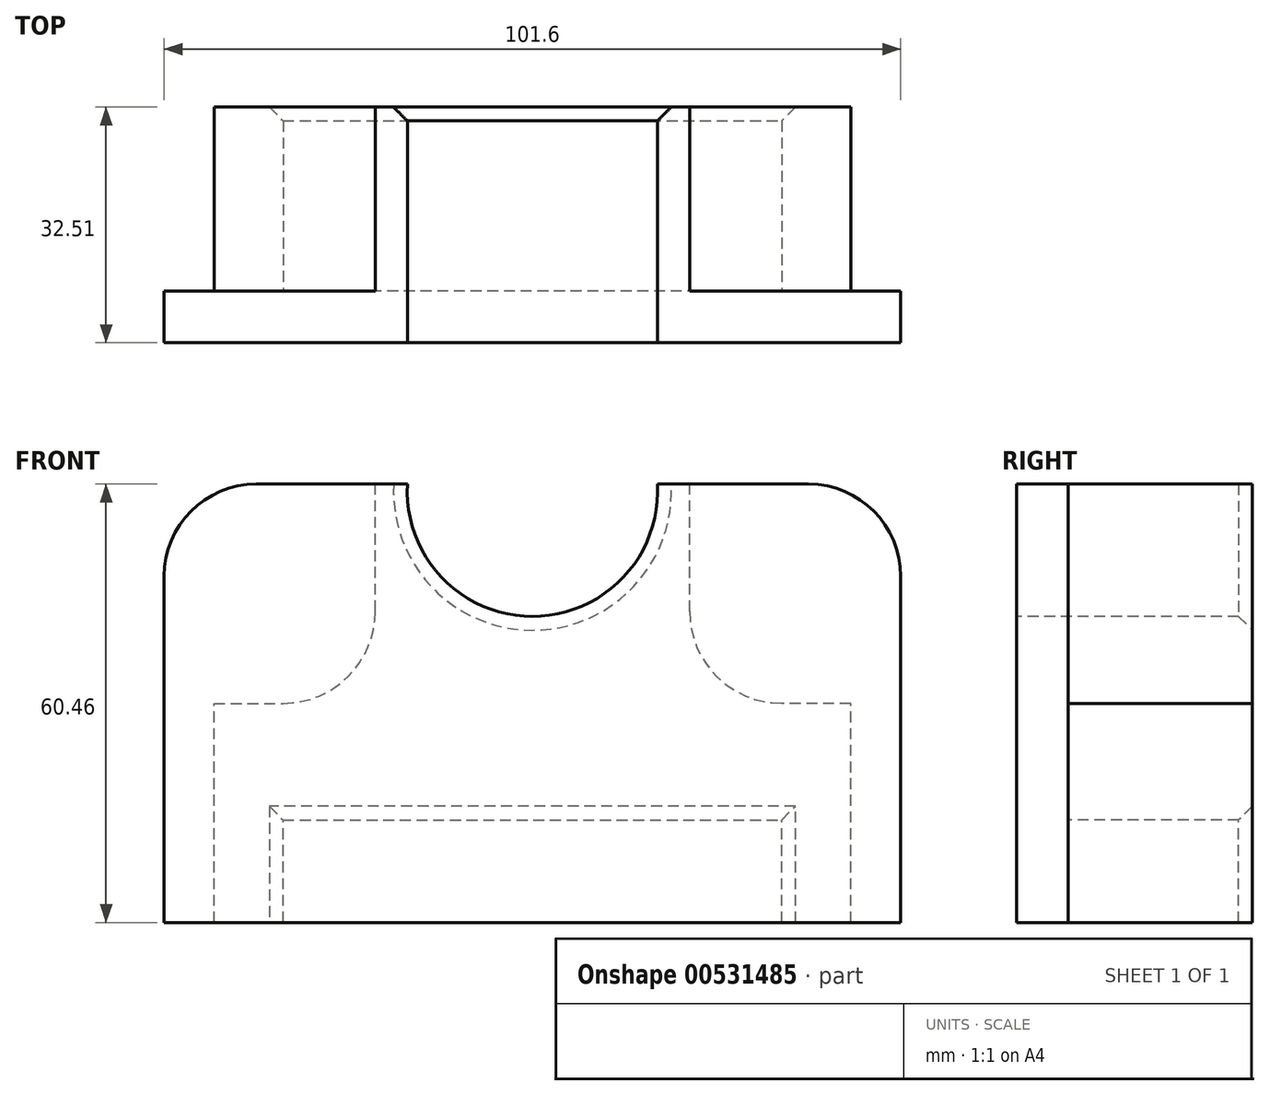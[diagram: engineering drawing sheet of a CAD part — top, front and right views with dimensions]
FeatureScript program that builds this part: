
annotation { "Feature Type Name" : "Feature", "Feature Type Description" : "" }
export const myFeature = defineFeature(function(context is Context, id is Id, definition is map)
    precondition{}
    {
        {
            var Q0;
            Q0=qCreatedBy(makeId("Front.planeOp"),FACE);
            var sketch = newSketch(context, id + "F0", { "sketchPlane" : qUnion([Q0])});
            skLineSegment(sketch, "E0.bottom", {"start": v(50.8, -30.23) * mm, "end": v(-50.8, -30.23) * mm});
            skLineSegment(sketch, "E0.top", {"start": v(38.1, 30.23) * mm, "end": v(-38.1, 30.23) * mm});
            skLineSegment(sketch, "E0.left", {"start": v(50.8, -30.23) * mm, "end": v(50.8, 17.53) * mm});
            skLineSegment(sketch, "E0.right", {"start": v(-50.8, -30.23) * mm, "end": v(-50.8, 17.53) * mm});
            skPoint(sketch, "E0.middle", {"position": v(0, 0) * mm});
            skPoint(sketch, "E1.visualSharp", {"position": v(50.8, 30.23) * mm});
            skArc(sketch, "E1.filletArc", {"start": v(50.8, 17.53) * mm, "mid": v(47.08, 26.51) * mm, "end": v(38.1, 30.23) * mm});
            skPoint(sketch, "E2.visualSharp", {"position": v(-50.8, 30.23) * mm});
            skArc(sketch, "E2.filletArc", {"start": v(-38.1, 30.23) * mm, "mid": v(-47.08, 26.51) * mm, "end": v(-50.8, 17.53) * mm});
            skSolve(sketch);
        }
        {
            var Q0;
            Q0=makeQuery(id+"F0.imprint","IMPRINT",FACE,{"disambiguationData":[TD([[makeQuery(id+"F0.imprint","IMPRINT",EDGE,{"derivedFrom":sQuery(id+"F0.wireOp",EDGE,"E0.bottom")}),-1.0]])]});
            extrude(context, id + "F1", {"entities" : qUnion([Q0]), "depth" : 7.11 * mm, "offsetDistance" : 25.4 * mm});
        }
        {
            var Q0;
            Q0=qCreatedBy(makeId("Front.planeOp"),FACE);
            var sketch = newSketch(context, id + "F2", { "sketchPlane" : qUnion([Q0])});
            skLineSegment(sketch, "E3", {"start": v(-43.9, -30.23) * mm, "end": v(-43.9, 0) * mm});
            skLineSegment(sketch, "E4", {"start": v(-43.9, 0) * mm, "end": v(-34.38, 0) * mm});
            skLineSegment(sketch, "E5", {"start": v(-21.68, 12.7) * mm, "end": v(-21.68, 30.23) * mm});
            skPoint(sketch, "E6.visualSharp", {"position": v(-21.68, 0) * mm});
            skArc(sketch, "E6.filletArc", {"start": v(-34.38, 0) * mm, "mid": v(-25.4, 3.72) * mm, "end": v(-21.68, 12.7) * mm});
            skLineSegment(sketch, "E7", {"start": v(-43.9, -30.23) * mm, "end": v(-34.38, -30.23) * mm});
            skLineSegment(sketch, "E8", {"start": v(-34.38, -30.23) * mm, "end": v(-34.38, -16.1) * mm});
            skLineSegment(sketch, "E9", {"start": v(-34.38, -16.1) * mm, "end": v(0, -16.1) * mm});
            skLineSegment(sketch, "E10", {"start": v(-21.68, 30.23) * mm, "end": v(-17.23, 30.23) * mm});
            skArc(sketch, "E11", {"start": v(-17.23, 30.23) * mm, "mid": v(-17.26, 29.26) * mm, "end": v(-17.23, 28.28) * mm});
            skPoint(sketch, "E11.second.point", {"position": v(0, 8.22) * mm});
            skArc(sketch, "E12.MirrorCS", {"start": v(17.23, 30.23) * mm, "mid": v(17.26, 29.26) * mm, "end": v(17.23, 28.28) * mm});
            skLineSegment(sketch, "E13.MirrorCS", {"start": v(21.68, 30.23) * mm, "end": v(17.23, 30.23) * mm});
            skLineSegment(sketch, "E14.MirrorCS", {"start": v(21.68, 12.7) * mm, "end": v(21.68, 30.23) * mm});
            skArc(sketch, "E15.MirrorCS", {"start": v(34.38, 0) * mm, "mid": v(25.4, 3.72) * mm, "end": v(21.68, 12.7) * mm});
            skLineSegment(sketch, "E16.MirrorCS", {"start": v(43.9, 0) * mm, "end": v(34.38, 0) * mm});
            skLineSegment(sketch, "E17.MirrorCS", {"start": v(43.9, -30.23) * mm, "end": v(43.9, 0) * mm});
            skLineSegment(sketch, "E18.MirrorCS", {"start": v(43.9, -30.23) * mm, "end": v(34.38, -30.23) * mm});
            skLineSegment(sketch, "E19.MirrorCS", {"start": v(34.38, -30.23) * mm, "end": v(34.38, -16.1) * mm});
            skLineSegment(sketch, "E20.MirrorCS", {"start": v(34.38, -16.1) * mm, "end": v(0, -16.1) * mm});
            skArc(sketch, "E21", {"start": v(-17.23, 30.23) * mm, "mid": v(0, 12) * mm, "end": v(17.23, 30.23) * mm});
            skSolve(sketch);
        }
        {
            var Q0;
            Q0=makeQuery(id+"F2.imprint","IMPRINT",FACE,{"disambiguationData":[TD([[makeQuery(id+"F2.imprint","IMPRINT",EDGE,{"derivedFrom":sQuery(id+"F2.wireOp",EDGE,"E3")}),-1.0]])]});
            extrude(context, id + "F3", {"entities" : qUnion([Q0]), "operationType" : NewBodyOperationType.ADD, "oppositeDirection" : true, "depth" : 25.4 * mm, "offsetDistance" : 25.4 * mm});
        }
        {
            var Q0;
            Q0=makeQuery(id+"F3.opExtrude","CAP_EDGE",EDGE,{"disambiguationData":[OSD([sQuery(id+"F2.wireOp",EDGE,"E19.MirrorCS")])],"isStart":false});
            var Q1;
            Q1=makeQuery(id+"F3.opExtrude","CAP_EDGE",EDGE,{"disambiguationData":[OSD([sQuery(id+"F2.wireOp",EDGE,"E9"),sQuery(id+"F2.wireOp",EDGE,"E20.MirrorCS")])],"isStart":false});
            var Q2;
            Q2=makeQuery(id+"F3.opExtrude","CAP_EDGE",EDGE,{"disambiguationData":[OSD([sQuery(id+"F2.wireOp",EDGE,"E8")])],"isStart":false});
            chamfer(context, id + "F4", {"entities" : qUnion([Q0, Q1, Q2]), "width" : 1.9 * mm, "tangentPropagation" : true});
        }
        {
            var Q0;
            {var subQ0=sQuery(id+"F0.wireOp",EDGE,"E0.top");Q0=makeQuery(id+"F3.boolean.opBoolean","SPLIT",FACE,{"disambiguationData":[TD([makeQuery(id+"F3.opExtrude","SWEPT_FACE",FACE,{"disambiguationData":[OSD([sQuery(id+"F2.wireOp",EDGE,"E21")])]})])],"derivedFrom":makeQuery(id+"F1.opExtrude","CAP_FACE",FACE,{"disambiguationData":[OSD([sQuery(id+"F0.wireOp",EDGE,"E0.bottom"),subQ0,sQuery(id+"F0.wireOp",EDGE,"E0.left"),sQuery(id+"F0.wireOp",EDGE,"E0.right"),sQuery(id+"F0.wireOp",EDGE,"E1.filletArc"),sQuery(id+"F0.wireOp",EDGE,"E2.filletArc")])],"isStart":true})});}
            extrude(context, id + "F5", {"entities" : qUnion([Q0]), "operationType" : NewBodyOperationType.REMOVE, "oppositeDirection" : true, "depth" : 25.4 * mm, "offsetDistance" : 25.4 * mm});
        }
        {
            var Q0;
            Q0=makeQuery(id+"F3.opExtrude","CAP_EDGE",EDGE,{"disambiguationData":[OSD([sQuery(id+"F2.wireOp",EDGE,"E21")])],"isStart":false});
            chamfer(context, id + "F6", {"entities" : qUnion([Q0]), "width" : 1.9 * mm, "tangentPropagation" : true});
        }
    });
